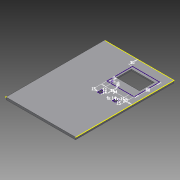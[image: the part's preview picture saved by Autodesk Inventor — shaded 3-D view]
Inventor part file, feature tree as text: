
AUTODESK INVENTOR PART (.ipt)
format: ipt  version: 2015 SP1 (Build 190203100, 203)  size: 122,880 bytes
history: native  units: mm
features: extrude x4, sketch x4
ambient origin geometry x8: Origin, YZ Plane, XZ Plane, XY Plane, X Axis, Y Axis, Z Axis, Center Point
bodies: Solid1 (feature_tree)
feature tree (8):
  extrude  "Extrusion1"  Depth=340.0mm
  sketch  "Sketch2"  dims[d2=8.0mm d3=0.0mm d4=94.0mm]
  extrude  "Extrusion2"  Depth=94.0mm
  extrude  "Extrusion3"  Depth=20.0mm
  extrude  "Extrusion4"  Depth=3.5mm
  sketch  "Sketch1"  dims[d0=240.0mm d1=340.0mm]
  sketch  "Sketch3"  dims[d5=88.0mm d6=20.0mm]
  sketch  "Sketch4"  dims[d7=30.0mm d8=9.0mm d9=9.0mm d10=8.0mm d11=11.0mm d12=14.0mm d13=11.0mm d14=14.0mm d15=15.0mm d16=15.0mm d17=35.0mm d18=4.0mm d19=0.0mm d20=94.0mm d21=30.0mm d22=88.0mm d23=20.0mm d24=3.5mm d25=0.0mm d26=8.0mm d27=7.0mm d28=10.0mm d29=27.0mm d30=3.5mm d31=0.0mm]
